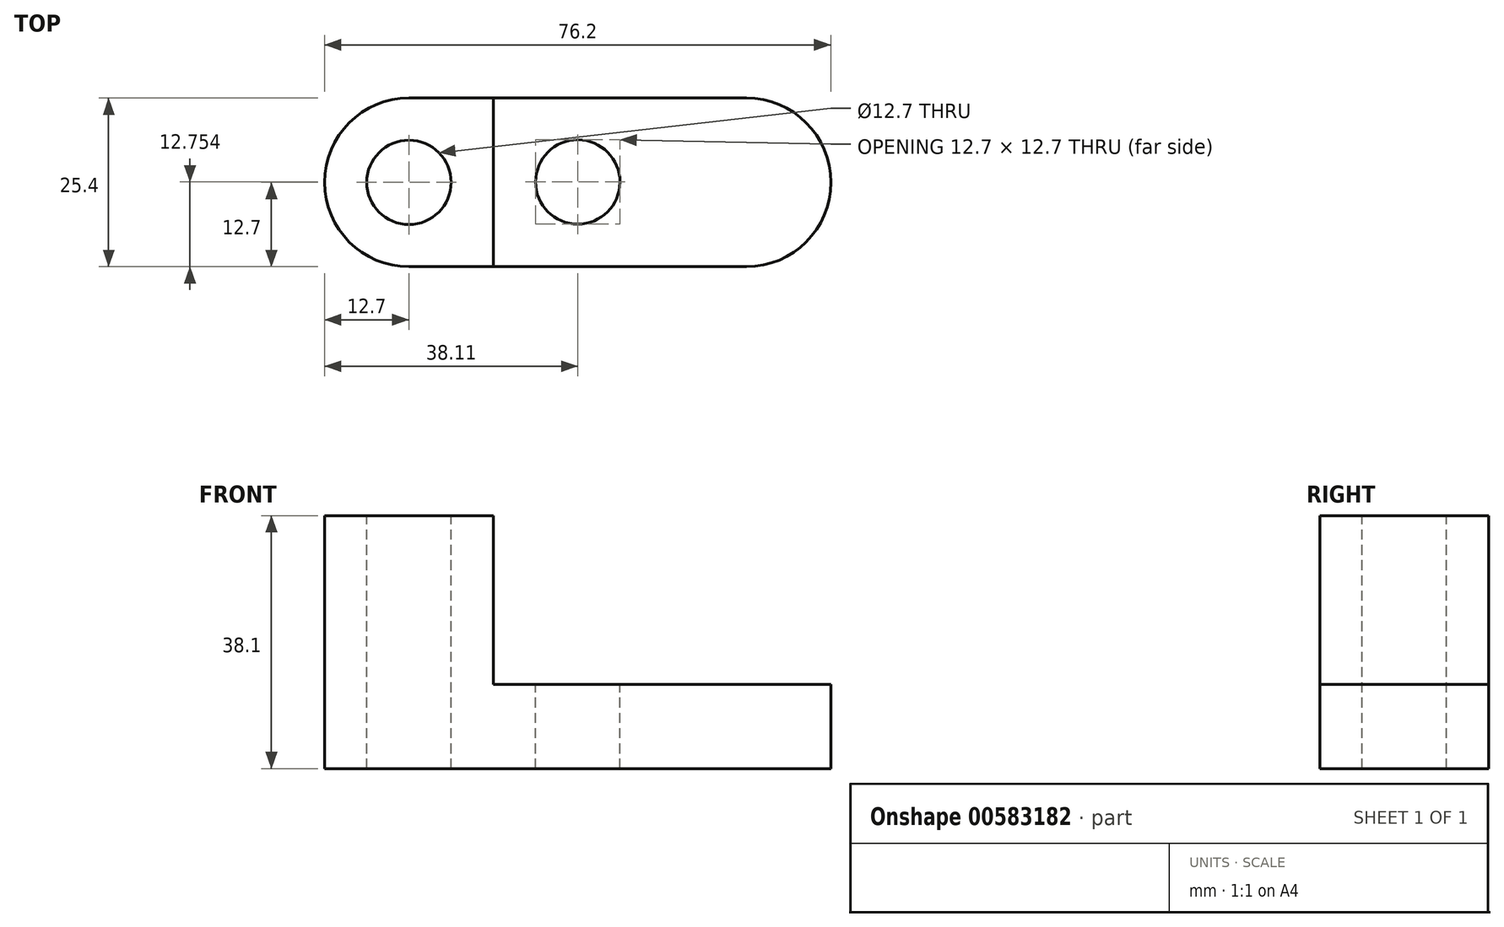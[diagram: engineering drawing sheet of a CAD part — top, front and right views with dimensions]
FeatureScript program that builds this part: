
annotation { "Feature Type Name" : "Feature", "Feature Type Description" : "" }
export const myFeature = defineFeature(function(context is Context, id is Id, definition is map)
    precondition{}
    {
        {
            var Q0;
            Q0=qCreatedBy(makeId("Front.planeOp"),FACE);
            var sketch = newSketch(context, id + "F0", { "sketchPlane" : qUnion([Q0])});
            skLineSegment(sketch, "E0.bottom", {"start": v(0, 0) * mm, "end": v(-76.2, 0) * mm});
            skLineSegment(sketch, "E0.top", {"start": v(0, 38.1) * mm, "end": v(-76.2, 38.1) * mm});
            skLineSegment(sketch, "E0.left", {"start": v(0, 0) * mm, "end": v(0, 38.1) * mm});
            skLineSegment(sketch, "E0.right", {"start": v(-76.2, 0) * mm, "end": v(-76.2, 38.1) * mm});
            skSolve(sketch);
        }
        {
            var Q0;
            Q0=makeQuery(id+"F0.imprint","IMPRINT",FACE,{"disambiguationData":[TD([[makeQuery(id+"F0.imprint","IMPRINT",EDGE,{"derivedFrom":sQuery(id+"F0.wireOp",EDGE,"E0.bottom")}),-1.0]])]});
            extrude(context, id + "F1", {"entities" : qUnion([Q0]), "depth" : 25.4 * mm, "offsetDistance" : 25.4 * mm});
        }
        {
            var Q0;
            Q0=makeQuery(id+"F1.opExtrude","CAP_FACE",FACE,{"disambiguationData":[OSD([sQuery(id+"F0.wireOp",EDGE,"E0.bottom"),sQuery(id+"F0.wireOp",EDGE,"E0.top"),sQuery(id+"F0.wireOp",EDGE,"E0.left"),sQuery(id+"F0.wireOp",EDGE,"E0.right")])],"isStart":false});
            var sketch = newSketch(context, id + "F2", { "sketchPlane" : qUnion([Q0])});
            skLineSegment(sketch, "E1", {"start": v(-76.2, 38.1) * mm, "end": v(-50.79, 38.1) * mm});
            skLineSegment(sketch, "E2", {"start": v(-50.79, 38.1) * mm, "end": v(-50.79, 12.7) * mm});
            skLineSegment(sketch, "E3", {"start": v(-50.79, 12.7) * mm, "end": v(0, 12.7) * mm});
            skSolve(sketch);
        }
        {
            var Q0;
            {var subQ0=sQuery(id+"F2.wireOp",EDGE,"E2");Q0=makeQuery(id+"F2.imprint","IMPRINT",FACE,{"disambiguationData":[TD([[makeQuery(id+"F2.imprint","IMPRINT",EDGE,{"derivedFrom":subQ0}),1.0]])]});}
            extrude(context, id + "F3", {"entities" : qUnion([Q0]), "operationType" : NewBodyOperationType.REMOVE, "endBound" : BoundingType.THROUGH_ALL, "oppositeDirection" : true, "depth" : 25.4 * mm, "offsetDistance" : 25.4 * mm});
        }
        {
            var Q0;
            Q0=makeQuery(id+"F3.boolean.opBoolean","COPY",FACE,{"derivedFrom":makeQuery(id+"F3.opExtrude","SWEPT_FACE",FACE,{"disambiguationData":[OSD([sQuery(id+"F2.wireOp",EDGE,"E3")])]})});
            var sketch = newSketch(context, id + "F4", { "sketchPlane" : qUnion([Q0])});
            skLineSegment(sketch, "E4", {"start": v(0, 0) * mm, "end": v(-12.7, 0) * mm});
            skArc(sketch, "E5", {"start": v(-12.7, -25.4) * mm, "mid": v(0, -12.7) * mm, "end": v(-12.7, 0) * mm});
            skSolve(sketch);
        }
        {
            var Q0;
            {var subQ0=sQuery(id+"F4.wireOp",EDGE,"E5");var subQ1=sQuery(id+"F2.wireOp",EDGE,"E3");var subQ2=makeQuery(id+"F3.boolean.opBoolean","COPY",EDGE,{"derivedFrom":makeQuery(id+"F3.opExtrude","CAP_EDGE",EDGE,{"disambiguationData":[OSD([subQ1])],"isStart":true})});var subQ3=makeQuery(id+"F4.imprint","INTERSECT",VERTEX,{"derivedFrom":[subQ2,subQ0]});Q0=makeQuery(id+"F4.imprint","IMPRINT",FACE,{"disambiguationData":[TD([[makeQuery(id+"F4.imprint","IMPRINT",EDGE,{"disambiguationData":[TD([[subQ3,-1.0]])],"derivedFrom":subQ0}),-1.0]])]});}
            var Q1;
            {var subQ0=sQuery(id+"F4.wireOp",EDGE,"E4");Q1=makeQuery(id+"F4.imprint","IMPRINT",FACE,{"disambiguationData":[TD([[makeQuery(id+"F4.imprint","IMPRINT",EDGE,{"derivedFrom":subQ0}),-1.0]])]});}
            extrude(context, id + "F5", {"entities" : qUnion([Q0, Q1]), "operationType" : NewBodyOperationType.REMOVE, "endBound" : BoundingType.THROUGH_ALL, "oppositeDirection" : true, "depth" : 25.4 * mm, "offsetDistance" : 25.4 * mm});
        }
        {
            var Q0;
            Q0=makeQuery(id+"F3.boolean.opBoolean","COPY",FACE,{"derivedFrom":makeQuery(id+"F3.opExtrude","SWEPT_FACE",FACE,{"disambiguationData":[OSD([sQuery(id+"F2.wireOp",EDGE,"E3")])]})});
            var sketch = newSketch(context, id + "F6", { "sketchPlane" : qUnion([Q0])});
            skCircle(sketch, "E6", {"center": v(-12.7, -12.7) * mm, "radius": 6.35 * mm});
            skCircle(sketch, "E7", {"center": v(-38.09, -12.65) * mm, "radius": 6.35 * mm});
            skLineSegment(sketch, "E8", {"start": v(-12.7, -6.35) * mm, "end": v(-38.09, -6.3) * mm});
            skLineSegment(sketch, "E9", {"start": v(-12.7, -19.05) * mm, "end": v(-38.09, -19) * mm});
            skSolve(sketch);
        }
        {
            var Q0;
            {var subQ0=sQuery(id+"F6.wireOp",EDGE,"E6");var subQ3=makeQuery(id+"F6.imprint","IMPRINT",VERTEX,{"derivedFrom":subQ0});Q0=makeQuery(id+"F6.imprint","IMPRINT",FACE,{"disambiguationData":[TD([[makeQuery(id+"F6.imprint","IMPRINT",EDGE,{"disambiguationData":[TD([[subQ3,1.0]])],"derivedFrom":subQ0}),1.0]])]});}
            var Q1;
            {var subQ0=sQuery(id+"F6.wireOp",EDGE,"E7");var subQ2=makeQuery(id+"F6.imprint","IMPRINT",VERTEX,{"derivedFrom":subQ0});Q1=makeQuery(id+"F6.imprint","IMPRINT",FACE,{"disambiguationData":[TD([[makeQuery(id+"F6.imprint","IMPRINT",EDGE,{"disambiguationData":[TD([[subQ2,1.0]])],"derivedFrom":subQ0}),1.0]])]});}
            var Q2;
            {var subQ0=sQuery(id+"F6.wireOp",EDGE,"E8");Q2=makeQuery(id+"F6.imprint","IMPRINT",FACE,{"disambiguationData":[TD([[makeQuery(id+"F6.imprint","IMPRINT",EDGE,{"derivedFrom":subQ0}),1.0]])]});}
            extrude(context, id + "F7", {"entities" : qUnion([Q0, Q1, Q2]), "operationType" : NewBodyOperationType.REMOVE, "endBound" : BoundingType.THROUGH_ALL, "oppositeDirection" : true, "depth" : 25.4 * mm, "offsetDistance" : 25.4 * mm});
        }
        {
            var Q0;
            Q0=makeQuery(id+"F1.opExtrude","SWEPT_FACE",FACE,{"disambiguationData":[OSD([sQuery(id+"F0.wireOp",EDGE,"E0.top")])]});
            var sketch = newSketch(context, id + "F8", { "sketchPlane" : qUnion([Q0])});
            skPoint(sketch, "E10.endSnap0", {"position": v(-50.79, -12.7) * mm});
            skCircle(sketch, "E11", {"center": v(-63.5, -12.7) * mm, "radius": 12.7 * mm});
            skSolve(sketch);
        }
        {
            var Q0;
            {var subQ0=sQuery(id+"F8.wireOp",EDGE,"E11");var subQ1=sQuery(id+"F0.wireOp",EDGE,"E0.top");var subQ4=makeQuery(id+"F1.opExtrude","CAP_EDGE",EDGE,{"disambiguationData":[OSD([subQ1])],"isStart":true});var subQ5=makeQuery(id+"F8.imprint","INTERSECT",VERTEX,{"derivedFrom":[subQ4,subQ0]});Q0=makeQuery(id+"F8.imprint","IMPRINT",FACE,{"disambiguationData":[TD([[makeQuery(id+"F8.imprint","IMPRINT",EDGE,{"disambiguationData":[TD([[subQ5,-1.0]])],"derivedFrom":subQ0}),-1.0]])]});}
            var Q1;
            {var subQ0=sQuery(id+"F8.wireOp",EDGE,"E11");var subQ1=sQuery(id+"F0.wireOp",EDGE,"E0.top");var subQ4=makeQuery(id+"F1.opExtrude","CAP_EDGE",EDGE,{"disambiguationData":[OSD([subQ1])],"isStart":false});var subQ5=makeQuery(id+"F8.imprint","INTERSECT",VERTEX,{"derivedFrom":[subQ4,subQ0]});Q1=makeQuery(id+"F8.imprint","IMPRINT",FACE,{"disambiguationData":[TD([[makeQuery(id+"F8.imprint","IMPRINT",EDGE,{"disambiguationData":[TD([[subQ5,1.0]])],"derivedFrom":subQ0}),-1.0]])]});}
            var Q2;
            {var subQ1=sQuery(id+"F0.wireOp",EDGE,"E0.top");var subQ6=makeQuery(id+"F3.boolean.opBoolean","COPY",EDGE,{"derivedFrom":makeQuery(id+"F3.opExtrude","SWEPT_EDGE",EDGE,{"disambiguationData":[OSD([subQ1,sQuery(id+"F2.wireOp",EDGE,"E1"),sQuery(id+"F2.wireOp",EDGE,"E2")])]})});Q2=makeQuery(id+"F8.imprint","IMPRINT",FACE,{"disambiguationData":[TD([[makeQuery(id+"F8.imprint","IMPRINT",EDGE,{"derivedFrom":subQ6}),-1.0]])]});}
            extrude(context, id + "F9", {"entities" : qUnion([Q0, Q1, Q2]), "operationType" : NewBodyOperationType.REMOVE, "oppositeDirection" : true, "depth" : 25.4 * mm, "offsetDistance" : 25.4 * mm});
        }
        {
            var Q0;
            {var subQ0=sQuery(id+"F0.wireOp",EDGE,"E0.top");var subQ1=makeQuery(id+"F1.opExtrude","CAP_EDGE",EDGE,{"disambiguationData":[OSD([subQ0])],"isStart":false});var subQ2=sQuery(id+"F0.wireOp",EDGE,"E0.right");var subQ3=makeQuery(id+"F1.opExtrude","SWEPT_EDGE",EDGE,{"disambiguationData":[OSD([subQ0,subQ2])]});var subQ4=makeQuery(id+"F8.imprint","INTERSECT",VERTEX,{"derivedFrom":[subQ3,subQ1]});var subQ5=sQuery(id+"F8.wireOp",EDGE,"E11");var subQ6=makeQuery(id+"F8.imprint","INTERSECT",VERTEX,{"derivedFrom":[subQ1,subQ5]});Q0=makeQuery(id+"F9.boolean.opBoolean","COPY",FACE,{"derivedFrom":makeQuery(id+"F9.opExtrude","CAP_FACE",FACE,{"disambiguationData":[OSD([subQ0,subQ2,subQ5]),TDD([makeQuery(id+"F8.imprint","IMPRINT",EDGE,{"disambiguationData":[TD([[subQ6,1.0]])],"derivedFrom":subQ5}),makeQuery(id+"F8.imprint","IMPRINT",EDGE,{"disambiguationData":[TD([[subQ4,-1.0]])],"derivedFrom":subQ3}),makeQuery(id+"F8.imprint","IMPRINT",EDGE,{"disambiguationData":[TD([[subQ6,-1.0]])],"derivedFrom":subQ1})])],"isStart":false})});}
            var Q1;
            {var subQ0=sQuery(id+"F0.wireOp",EDGE,"E0.top");var subQ1=makeQuery(id+"F1.opExtrude","CAP_EDGE",EDGE,{"disambiguationData":[OSD([subQ0])],"isStart":true});var subQ2=sQuery(id+"F0.wireOp",EDGE,"E0.right");var subQ3=makeQuery(id+"F1.opExtrude","SWEPT_EDGE",EDGE,{"disambiguationData":[OSD([subQ0,subQ2])]});var subQ4=makeQuery(id+"F8.imprint","INTERSECT",VERTEX,{"derivedFrom":[subQ3,subQ1]});var subQ5=sQuery(id+"F8.wireOp",EDGE,"E11");var subQ6=makeQuery(id+"F8.imprint","INTERSECT",VERTEX,{"derivedFrom":[subQ1,subQ5]});Q1=makeQuery(id+"F9.boolean.opBoolean","COPY",FACE,{"derivedFrom":makeQuery(id+"F9.opExtrude","CAP_FACE",FACE,{"disambiguationData":[OSD([subQ0,subQ2,subQ5]),TDD([makeQuery(id+"F8.imprint","IMPRINT",EDGE,{"disambiguationData":[TD([[subQ6,-1.0]])],"derivedFrom":subQ5}),makeQuery(id+"F8.imprint","IMPRINT",EDGE,{"disambiguationData":[TD([[subQ4,1.0]])],"derivedFrom":subQ3}),makeQuery(id+"F8.imprint","IMPRINT",EDGE,{"disambiguationData":[TD([[subQ6,-1.0]])],"derivedFrom":subQ1})])],"isStart":false})});}
            extrude(context, id + "F10", {"entities" : qUnion([Q0, Q1]), "operationType" : NewBodyOperationType.REMOVE, "oppositeDirection" : true, "depth" : 25.4 * mm, "offsetDistance" : 25.4 * mm});
        }
        {
            var Q0;
            Q0=makeQuery(id+"F1.opExtrude","SWEPT_FACE",FACE,{"disambiguationData":[OSD([sQuery(id+"F0.wireOp",EDGE,"E0.top")])]});
            var sketch = newSketch(context, id + "F11", { "sketchPlane" : qUnion([Q0])});
            skCircle(sketch, "E12", {"center": v(-63.5, -12.7) * mm, "radius": 6.35 * mm});
            skSolve(sketch);
        }
        {
            var Q0;
            Q0=makeQuery(id+"F11.imprint","IMPRINT",FACE,{"disambiguationData":[TD([[makeQuery(id+"F11.imprint","IMPRINT",EDGE,{"derivedFrom":sQuery(id+"F11.wireOp",EDGE,"E12")}),1.0]])]});
            extrude(context, id + "F12", {"entities" : qUnion([Q0]), "operationType" : NewBodyOperationType.REMOVE, "endBound" : BoundingType.THROUGH_ALL, "oppositeDirection" : true, "depth" : 25.4 * mm, "offsetDistance" : 25.4 * mm});
        }
    });
